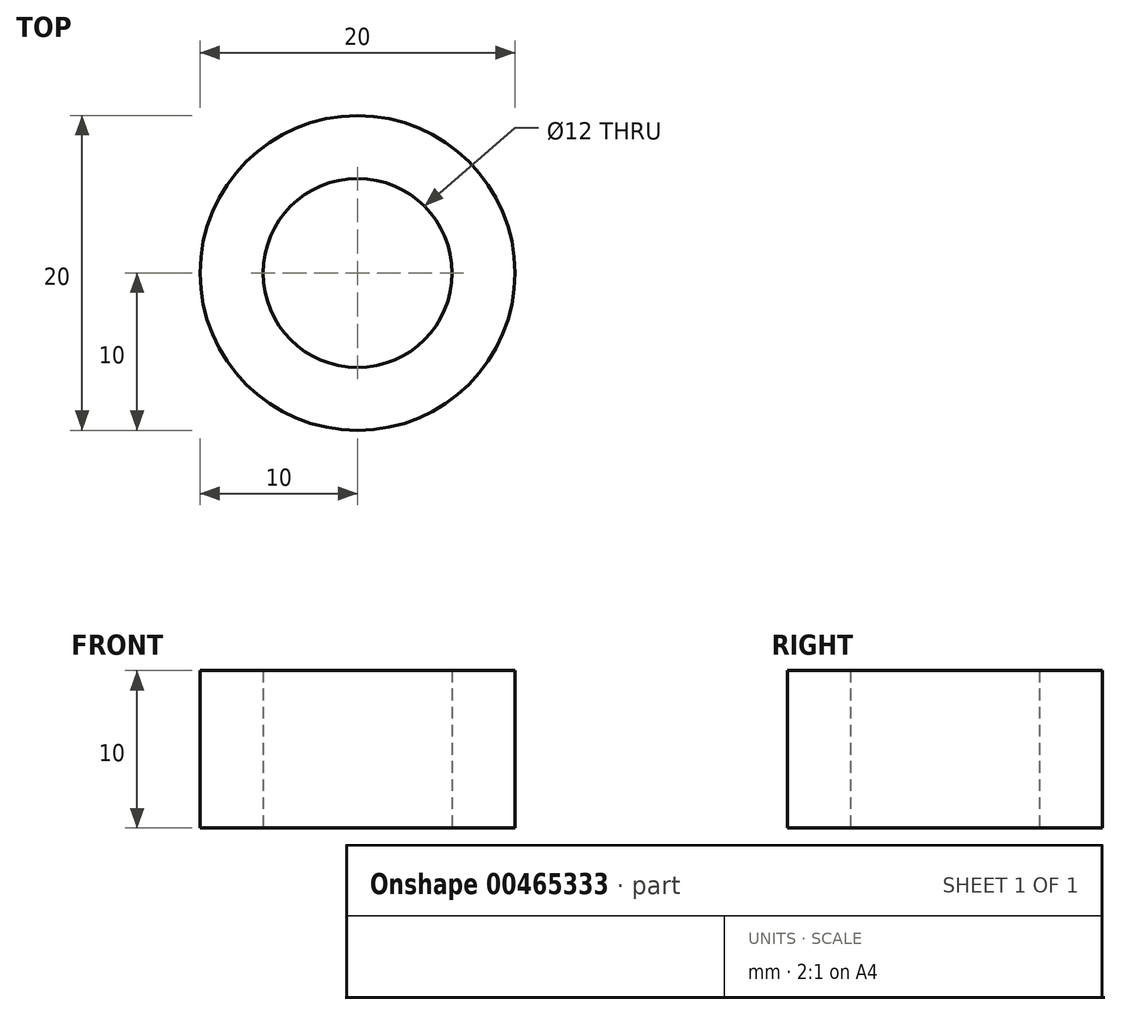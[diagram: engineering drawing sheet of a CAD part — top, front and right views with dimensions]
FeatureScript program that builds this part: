
annotation { "Feature Type Name" : "Feature", "Feature Type Description" : "" }
export const myFeature = defineFeature(function(context is Context, id is Id, definition is map)
    precondition{}
    {
        {
            var Q0;
            Q0=qCreatedBy(makeId("Top.planeOp"),FACE);
            var sketch = newSketch(context, id + "F0", { "sketchPlane" : qUnion([Q0])});
            skCircle(sketch, "E0", {"center": v(0, 0) * mm, "radius": 10 * mm});
            skCircle(sketch, "E1", {"center": v(0, 0) * mm, "radius": 6 * mm});
            skSolve(sketch);
        }
        {
            var Q0;
            Q0 = qSketchRegion(id + "F0", true);
            extrude(context, id + "F1", {"entities" : qUnion([Q0]), "depth" : 10 * mm});
        }
    });
